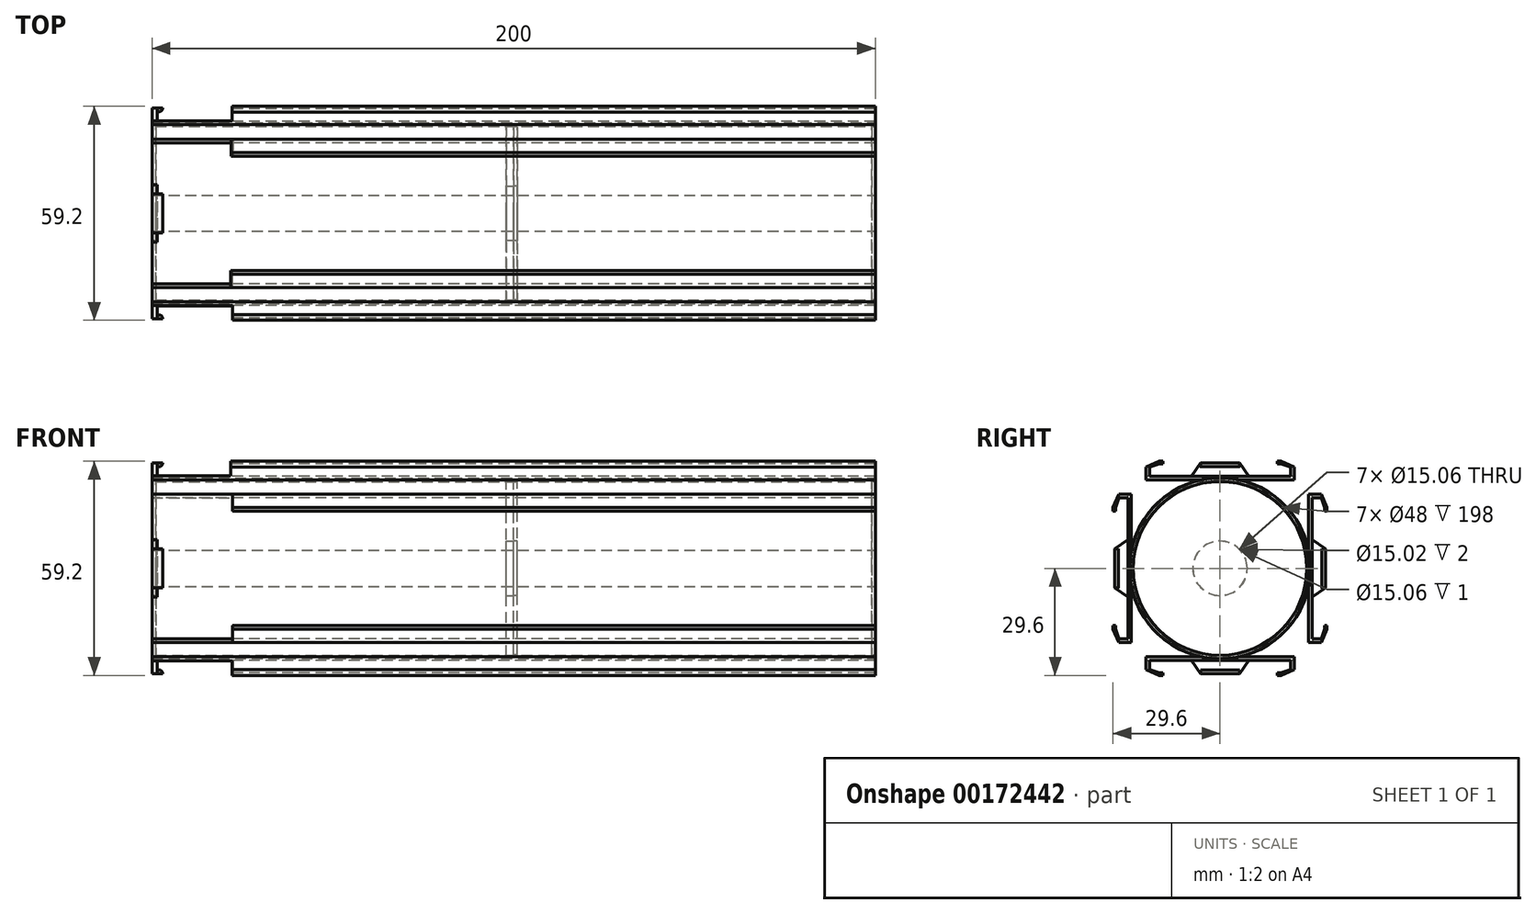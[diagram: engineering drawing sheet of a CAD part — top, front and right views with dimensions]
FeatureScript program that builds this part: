
annotation { "Feature Type Name" : "Feature", "Feature Type Description" : "" }
export const myFeature = defineFeature(function(context is Context, id is Id, definition is map)
    precondition{}
    {
        {
            var Q0;
            Q0=qCreatedBy(makeId("Top.planeOp"),FACE);
            var sketch = newSketch(context, id + "F0", { "sketchPlane" : qUnion([Q0])});
            skLineSegment(sketch, "E0", {"start": v(-100, 0) * mm, "end": v(-100, 25) * mm});
            skLineSegment(sketch, "E1", {"start": v(-100, 25) * mm, "end": v(100, 25) * mm});
            skLineSegment(sketch, "E2", {"start": v(100, 25) * mm, "end": v(100, 0) * mm});
            skLineSegment(sketch, "E3", {"start": v(100, 0) * mm, "end": v(-100, 0) * mm});
            skSolve(sketch);
        }
        {
            var Q0;
            Q0=makeQuery(id+"F0.imprint","IMPRINT",FACE,{"disambiguationData":[TD([[makeQuery(id+"F0.imprint","IMPRINT",EDGE,{"derivedFrom":sQuery(id+"F0.wireOp",EDGE,"E0")}),-1.0]])]});
            var Q1;
            Q1=sQuery(id+"F0.wireOp",EDGE,"E3");
            revolve(context, id + "F1", {"entities" : qUnion([Q0]), "axis" : qUnion([Q1]), "revolveType" : RevolveType.FULL});
        }
        {
            var Q0;
            Q0=qCreatedBy(makeId("Right.planeOp"),FACE);
            var sketch = newSketch(context, id + "F2", { "sketchPlane" : qUnion([Q0])});
            skLineSegment(sketch, "E4.top", {"start": v(20.5, 24.5) * mm, "end": v(-20.5, 24.5) * mm});
            skLineSegment(sketch, "E4.left", {"start": v(20.5, 28) * mm, "end": v(20.5, 24.5) * mm});
            skPoint(sketch, "E4.middle", {"position": v(0, 26.25) * mm});
            skLineSegment(sketch, "E5", {"start": v(19.5, 25.5) * mm, "end": v(0, 25.5) * mm});
            skLineSegment(sketch, "E6", {"start": v(19.5, 25.5) * mm, "end": v(19.5, 28) * mm});
            skLineSegment(sketch, "E7", {"start": v(20.93, 29.6) * mm, "end": v(1.4, 29.6) * mm, "construction": true});
            skLineSegment(sketch, "E8", {"start": v(20.5, 28) * mm, "end": v(16.8, 29.6) * mm});
            skLineSegment(sketch, "E9", {"start": v(16.8, 28.9) * mm, "end": v(19.5, 28) * mm});
            skLineSegment(sketch, "E10", {"start": v(16.8, 28.9) * mm, "end": v(22.6, 28.9) * mm, "construction": true});
            skLineSegment(sketch, "E11.MirrorCS", {"start": v(-19.5, 25.5) * mm, "end": v(0, 25.5) * mm});
            skLineSegment(sketch, "E12.MirrorCS", {"start": v(-16.8, 28.9) * mm, "end": v(-19.5, 28) * mm});
            skLineSegment(sketch, "E13.MirrorCS", {"start": v(-20.5, 28) * mm, "end": v(-16.8, 29.6) * mm});
            skLineSegment(sketch, "E14.MirrorCS", {"start": v(-20.5, 28) * mm, "end": v(-20.5, 24.5) * mm});
            skLineSegment(sketch, "E15.MirrorCS", {"start": v(-19.5, 25.5) * mm, "end": v(-19.5, 28) * mm});
            skLineSegment(sketch, "E16", {"start": v(16.87, 25.5) * mm, "end": v(16.8, 28.9) * mm, "construction": true});
            skLineSegment(sketch, "E17", {"start": v(16.8, 28.9) * mm, "end": v(15.8, 28.9) * mm});
            skLineSegment(sketch, "E18", {"start": v(15.8, 28.9) * mm, "end": v(15.8, 29.6) * mm});
            skLineSegment(sketch, "E19", {"start": v(15.8, 29.6) * mm, "end": v(16.8, 29.6) * mm});
            skLineSegment(sketch, "E20.MirrorCS", {"start": v(-20.93, 29.6) * mm, "end": v(-1.4, 29.6) * mm, "construction": true});
            skLineSegment(sketch, "E21.MirrorCS", {"start": v(-15.8, 28.9) * mm, "end": v(-15.8, 29.6) * mm});
            skLineSegment(sketch, "E22.MirrorCS", {"start": v(-16.8, 28.9) * mm, "end": v(-15.8, 28.9) * mm});
            skLineSegment(sketch, "E23", {"start": v(-15.8, 29.6) * mm, "end": v(-16.8, 29.6) * mm});
            skSolve(sketch);
        }
        {
            var Q0;
            Q0 = qSketchRegion(id + "F2", true);
            extrude(context, id + "F3", {"entities" : qUnion([Q0]), "operationType" : NewBodyOperationType.ADD, "endBound" : BoundingType.SYMMETRIC, "depth" : 200 * mm});
        }
        {
            var Q0;
            Q0=makeQuery(id+"F1.opRevolve","SWEPT_FACE",FACE,{"disambiguationData":[OSD([sQuery(id+"F0.wireOp",EDGE,"E0")])]});
            shell(context, id + "F4", {"entities" : qUnion([Q0]), "thickness" : 1 * mm});
        }
        {
            var Q0;
            Q0=qCreatedBy(makeId("Right.planeOp"),FACE);
            var sketch = newSketch(context, id + "F5", { "sketchPlane" : qUnion([Q0])});
            skCircle(sketch, "E24", {"center": v(0, 0) * mm, "radius": 24.27 * mm});
            skSolve(sketch);
        }
        {
            var Q0;
            Q0 = qSketchRegion(id + "F5", true);
            extrude(context, id + "F6", {"entities" : qUnion([Q0]), "oppositeDirection" : true, "depth" : 2 * mm});
        }
        {
            var Q0;
            Q0=makeQuery(id+"F6.opExtrude","CAP_FACE",FACE,{"disambiguationData":[OSD([sQuery(id+"F5.wireOp",EDGE,"E24")])],"isStart":true});
            var sketch = newSketch(context, id + "F7", { "sketchPlane" : qUnion([Q0])});
            skCircle(sketch, "E25", {"center": v(0, 0) * mm, "radius": 7.51 * mm});
            skSolve(sketch);
        }
        {
            var Q0;
            Q0 = qSketchRegion(id + "F7", true);
            extrude(context, id + "F8", {"entities" : qUnion([Q0]), "operationType" : NewBodyOperationType.REMOVE, "oppositeDirection" : true, "depth" : 5 * mm});
        }
        {
            var Q0;
            Q0=makeQuery(id+"F3.opExtrude","CAP_FACE",FACE,{"disambiguationData":[OSD([sQuery(id+"F2.wireOp",EDGE,"E4.top"),sQuery(id+"F2.wireOp",EDGE,"E4.left"),sQuery(id+"F2.wireOp",EDGE,"E5"),sQuery(id+"F2.wireOp",EDGE,"E6"),sQuery(id+"F2.wireOp",EDGE,"E8"),sQuery(id+"F2.wireOp",EDGE,"ZNRFgcwy-b1ID-LXQQ-LieV-oTXK7mRWD8L2"),sQuery(id+"F2.wireOp",EDGE,"E9"),sQuery(id+"F2.wireOp",EDGE,"E11.MirrorCS"),sQuery(id+"F2.wireOp",EDGE,"E12.MirrorCS"),sQuery(id+"F2.wireOp",EDGE,"bf2c11c1-d9c3-4b4b-aa85-f261bc206fdc0.MirrorCS"),sQuery(id+"F2.wireOp",EDGE,"E13.MirrorCS"),sQuery(id+"F2.wireOp",EDGE,"E14.MirrorCS"),sQuery(id+"F2.wireOp",EDGE,"E15.MirrorCS")])],"isStart":true});
            var sketch = newSketch(context, id + "F9", { "sketchPlane" : qUnion([Q0])});
            skLineSegment(sketch, "E26", {"start": v(0, 29.1) * mm, "end": v(-5.4, 29.1) * mm});
            skLineSegment(sketch, "E27", {"start": v(-5.4, 29.1) * mm, "end": v(-7.94, 25.5) * mm});
            skLineSegment(sketch, "E28.MirrorCS", {"start": v(0, 29.1) * mm, "end": v(5.4, 29.1) * mm});
            skLineSegment(sketch, "E29.MirrorCS", {"start": v(5.4, 29.1) * mm, "end": v(7.94, 25.5) * mm});
            skLineSegment(sketch, "E30", {"start": v(-7.94, 25.5) * mm, "end": v(7.94, 25.5) * mm});
            skSolve(sketch);
        }
        {
            var Q0;
            Q0=qCreatedBy(makeId("Right.planeOp"),FACE);
            var sketch = newSketch(context, id + "F10", { "sketchPlane" : qUnion([Q0])});
            skCircle(sketch, "E31", {"center": v(0, 0) * mm, "radius": 23.91 * mm});
            skSolve(sketch);
        }
        {
            var Q0;
            Q0 = qSketchRegion(id + "F10", true);
            extrude(context, id + "F11", {"entities" : qUnion([Q0]), "operationType" : NewBodyOperationType.ADD, "depth" : 1 * mm});
        }
        {
            var Q0;
            Q0=qCreatedBy(makeId("Right.planeOp"),FACE);
            var sketch = newSketch(context, id + "F12", { "sketchPlane" : qUnion([Q0])});
            skCircle(sketch, "E32", {"center": v(0, 0) * mm, "radius": 7.53 * mm});
            skSolve(sketch);
        }
        {
            var Q0;
            Q0 = qSketchRegion(id + "F12", true);
            extrude(context, id + "F13", {"entities" : qUnion([Q0]), "operationType" : NewBodyOperationType.REMOVE, "depth" : 2 * mm});
        }
        {
            var Q0;
            Q0=makeQuery(id+"F4.opShell","OFFSET_FACE",FACE,{"disambiguationData":[OSD([sQuery(id+"F0.wireOp",EDGE,"E2")])]});
            extrude(context, id + "F14", {"entities" : qUnion([Q0]), "oppositeDirection" : true, "depth" : 1 * mm});
        }
        {
            var Q0;
            Q0=makeQuery(id+"F1.opRevolve","SWEPT_FACE",FACE,{"disambiguationData":[OSD([sQuery(id+"F0.wireOp",EDGE,"E2")])]});
            var sketch = newSketch(context, id + "F15", { "sketchPlane" : qUnion([Q0])});
            skCircle(sketch, "E33", {"center": v(0, 0) * mm, "radius": 24.05 * mm});
            skSolve(sketch);
        }
        {
            var Q0;
            Q0 = qSketchRegion(id + "F15", true);
            extrude(context, id + "F16", {"entities" : qUnion([Q0]), "oppositeDirection" : true, "depth" : 1 * mm});
        }
        {
            var Q0;
            Q0=makeQuery(id+"F1.opRevolve","SWEPT_FACE",FACE,{"disambiguationData":[OSD([sQuery(id+"F0.wireOp",EDGE,"E0")])]});
            var sketch = newSketch(context, id + "F17", { "sketchPlane" : qUnion([Q0])});
            skCircle(sketch, "E34", {"center": v(0, 0) * mm, "radius": 24.2 * mm});
            skSolve(sketch);
        }
        {
            var Q0;
            Q0 = qSketchRegion(id + "F17", true);
            extrude(context, id + "F18", {"entities" : qUnion([Q0]), "operationType" : NewBodyOperationType.ADD, "oppositeDirection" : true, "depth" : 1 * mm});
        }
        {
            var Q0;
            Q0=makeQuery(id+"F18.boolean.opBoolean","MERGE",FACE,{"derivedFrom":[makeQuery(id+"F1.opRevolve","SWEPT_FACE",FACE,{"disambiguationData":[OSD([sQuery(id+"F0.wireOp",EDGE,"E0")])]}),makeQuery(id+"F18.opExtrude","CAP_FACE",FACE,{"disambiguationData":[OSD([sQuery(id+"F17.wireOp",EDGE,"E34")])],"isStart":true})]});
            var sketch = newSketch(context, id + "F19", { "sketchPlane" : qUnion([Q0])});
            skCircle(sketch, "E35", {"center": v(0, 0) * mm, "radius": 7.53 * mm});
            skSolve(sketch);
        }
        {
            var Q0;
            Q0 = qSketchRegion(id + "F19", true);
            extrude(context, id + "F20", {"entities" : qUnion([Q0]), "operationType" : NewBodyOperationType.REMOVE, "oppositeDirection" : true, "depth" : 2 * mm});
        }
        {
            var Q0;
            Q0 = qSketchRegion(id + "F9", true);
            extrude(context, id + "F21", {"entities" : qUnion([Q0]), "operationType" : NewBodyOperationType.ADD, "oppositeDirection" : true, "depth" : 1.5 * mm});
        }
        {
            var Q0;
            Q0=makeQuery(id+"F21.opExtrude","SWEPT_FACE",FACE,{"disambiguationData":[OSD([sQuery(id+"F9.wireOp",EDGE,"E26"),sQuery(id+"F9.wireOp",EDGE,"E28.MirrorCS")])]});
            var sketch = newSketch(context, id + "F22", { "sketchPlane" : qUnion([Q0])});
            skPoint(sketch, "E36.oppositeSnap0", {"position": v(-99.25, -5.4) * mm});
            skLineSegment(sketch, "E36.bottom", {"start": v(-100, 5.4) * mm, "end": v(-97.07, 5.4) * mm});
            skLineSegment(sketch, "E36.top", {"start": v(-100, -5.4) * mm, "end": v(-97.07, -5.4) * mm});
            skLineSegment(sketch, "E36.left", {"start": v(-100, 5.4) * mm, "end": v(-100, -5.4) * mm});
            skLineSegment(sketch, "E36.right", {"start": v(-97.07, 5.4) * mm, "end": v(-97.07, -5.4) * mm});
            skSolve(sketch);
        }
        {
            var Q0;
            Q0 = qSketchRegion(id + "F22", true);
            extrude(context, id + "F23", {"entities" : qUnion([Q0]), "operationType" : NewBodyOperationType.ADD, "oppositeDirection" : true, "depth" : 1 * mm});
        }
        {
            var Q0;
            Q0=makeQuery(id+"F23.opExtrude","CAP_EDGE",EDGE,{"disambiguationData":[OSD([sQuery(id+"F22.wireOp",EDGE,"E36.right")])],"isStart":false});
            fillet(context, id + "F24", {"entities" : qUnion([Q0]), "radius" : 1 * mm, "tangentPropagation" : true, "allowEdgeOverflow" : false});
        }
        {
            var Q0;
            Q0=makeQuery(id+"F14.opExtrude","SWEPT_BODY",BODY,{"disambiguationData":[OSD([sQuery(id+"F0.wireOp",EDGE,"E2"),sQuery(id+"F2.wireOp",EDGE,"E4.top"),sQuery(id+"F2.wireOp",EDGE,"E4.left"),sQuery(id+"F2.wireOp",EDGE,"E5"),sQuery(id+"F2.wireOp",EDGE,"E6"),sQuery(id+"F2.wireOp",EDGE,"E8"),sQuery(id+"F2.wireOp",EDGE,"ZNRFgcwy-b1ID-LXQQ-LieV-oTXK7mRWD8L2"),sQuery(id+"F2.wireOp",EDGE,"E9"),sQuery(id+"F2.wireOp",EDGE,"E11.MirrorCS"),sQuery(id+"F2.wireOp",EDGE,"E12.MirrorCS"),sQuery(id+"F2.wireOp",EDGE,"bf2c11c1-d9c3-4b4b-aa85-f261bc206fdc0.MirrorCS"),sQuery(id+"F2.wireOp",EDGE,"E13.MirrorCS"),sQuery(id+"F2.wireOp",EDGE,"E14.MirrorCS"),sQuery(id+"F2.wireOp",EDGE,"E15.MirrorCS")])]});
            var Q1;
            Q1=makeQuery(id+"F1.opRevolve","SWEPT_BODY",BODY,{"disambiguationData":[OSD([sQuery(id+"F0.wireOp",EDGE,"E0"),sQuery(id+"F0.wireOp",EDGE,"E1"),sQuery(id+"F0.wireOp",EDGE,"E2"),sQuery(id+"F0.wireOp",EDGE,"E3")])]});
            var Q2;
            Q2=makeQuery(id+"F1.opRevolve","SWEPT_FACE",FACE,{"disambiguationData":[OSD([sQuery(id+"F0.wireOp",EDGE,"E1")])]});
            circularPattern(context, id + "F25", {"entities" : qUnion([Q0, Q1]), "axis" : qUnion([Q2]), "angle" : 360 * degree, "instanceCount" : 4});
        }
        {
            var Q0;
            Q0=makeQuery(id+"F1.opRevolve","SWEPT_BODY",BODY,{"disambiguationData":[OSD([sQuery(id+"F0.wireOp",EDGE,"E0"),sQuery(id+"F0.wireOp",EDGE,"E1"),sQuery(id+"F0.wireOp",EDGE,"E2"),sQuery(id+"F0.wireOp",EDGE,"E3")])]});
            var Q1;
            Q1=makeQuery(id+"F1.opRevolve","SWEPT_FACE",FACE,{"disambiguationData":[OSD([sQuery(id+"F0.wireOp",EDGE,"E1")])]});
            circularPattern(context, id + "F26", {"entities" : qUnion([Q0]), "axis" : qUnion([Q1]), "angle" : 360 * degree, "instanceCount" : 4, "equalSpace" : true});
        }
        {
            var Q0;
            Q0=makeQuery(id+"F3.opExtrude","SWEPT_FACE",FACE,{"disambiguationData":[OSD([sQuery(id+"F2.wireOp",EDGE,"E14.MirrorCS")])]});
            var sketch = newSketch(context, id + "F27", { "sketchPlane" : qUnion([Q0])});
            skLineSegment(sketch, "E37.bottom", {"start": v(-100.21, 30.33) * mm, "end": v(-78.25, 30.33) * mm});
            skLineSegment(sketch, "E37.top", {"start": v(-100.21, 25.63) * mm, "end": v(-78.25, 25.63) * mm});
            skLineSegment(sketch, "E37.left", {"start": v(-100.21, 30.33) * mm, "end": v(-100.21, 25.63) * mm});
            skLineSegment(sketch, "E37.right", {"start": v(-78.25, 30.33) * mm, "end": v(-78.25, 25.63) * mm});
            skSolve(sketch);
        }
        {
            var Q0;
            Q0 = qSketchRegion(id + "F27", true);
            extrude(context, id + "F28", {"entities" : qUnion([Q0]), "operationType" : NewBodyOperationType.REMOVE, "oppositeDirection" : true, "depth" : 6 * mm});
        }
        {
            var Q0;
            Q0=makeQuery(id+"F3.opExtrude","SWEPT_FACE",FACE,{"disambiguationData":[OSD([sQuery(id+"F2.wireOp",EDGE,"E4.left")])]});
            var sketch = newSketch(context, id + "F29", { "sketchPlane" : qUnion([Q0])});
            skLineSegment(sketch, "E38.bottom", {"start": v(100, 25.6) * mm, "end": v(78.07, 25.6) * mm});
            skLineSegment(sketch, "E38.top", {"start": v(100, 29.9) * mm, "end": v(78.07, 29.9) * mm});
            skLineSegment(sketch, "E38.left", {"start": v(100, 25.6) * mm, "end": v(100, 29.9) * mm});
            skLineSegment(sketch, "E38.right", {"start": v(78.07, 25.6) * mm, "end": v(78.07, 29.9) * mm});
            skSolve(sketch);
        }
        {
            var Q0;
            Q0 = qSketchRegion(id + "F29", true);
            extrude(context, id + "F30", {"entities" : qUnion([Q0]), "operationType" : NewBodyOperationType.REMOVE, "oppositeDirection" : true, "depth" : 5 * mm});
        }
        {
            var Q0;
            Q0=makeQuery(id+"F26.opPattern","COPY",FACE,{"derivedFrom":makeQuery(id+"F3.opExtrude","SWEPT_FACE",FACE,{"disambiguationData":[OSD([sQuery(id+"F2.wireOp",EDGE,"E14.MirrorCS")])]}),"instanceName":"2"});
            var sketch = newSketch(context, id + "F31", { "sketchPlane" : qUnion([Q0])});
            skLineSegment(sketch, "E39.bottom", {"start": v(100, -25.5) * mm, "end": v(77.62, -25.5) * mm});
            skLineSegment(sketch, "E39.top", {"start": v(100, -29.75) * mm, "end": v(77.62, -29.75) * mm});
            skLineSegment(sketch, "E39.left", {"start": v(100, -25.5) * mm, "end": v(100, -29.75) * mm});
            skLineSegment(sketch, "E39.right", {"start": v(77.62, -25.5) * mm, "end": v(77.62, -29.75) * mm});
            skSolve(sketch);
        }
        {
            var Q0;
            Q0 = qSketchRegion(id + "F31", true);
            extrude(context, id + "F32", {"entities" : qUnion([Q0]), "operationType" : NewBodyOperationType.REMOVE, "oppositeDirection" : true, "depth" : 5 * mm});
        }
        {
            var Q0;
            Q0=makeQuery(id+"F26.opPattern","COPY",FACE,{"derivedFrom":makeQuery(id+"F3.opExtrude","SWEPT_FACE",FACE,{"disambiguationData":[OSD([sQuery(id+"F2.wireOp",EDGE,"E4.left")])]}),"instanceName":"2"});
            var sketch = newSketch(context, id + "F33", { "sketchPlane" : qUnion([Q0])});
            skLineSegment(sketch, "E40.bottom", {"start": v(-100, -25.57) * mm, "end": v(-77.86, -25.57) * mm});
            skLineSegment(sketch, "E40.top", {"start": v(-100, -30.06) * mm, "end": v(-77.86, -30.06) * mm});
            skLineSegment(sketch, "E40.left", {"start": v(-100, -25.57) * mm, "end": v(-100, -30.06) * mm});
            skLineSegment(sketch, "E40.right", {"start": v(-77.86, -25.57) * mm, "end": v(-77.86, -30.06) * mm});
            skSolve(sketch);
        }
        {
            var Q0;
            Q0 = qSketchRegion(id + "F33", true);
            extrude(context, id + "F34", {"entities" : qUnion([Q0]), "operationType" : NewBodyOperationType.REMOVE, "oppositeDirection" : true, "depth" : 5 * mm});
        }
        {
            var Q0;
            Q0=makeQuery(id+"F26.opPattern","COPY",FACE,{"derivedFrom":makeQuery(id+"F3.opExtrude","SWEPT_FACE",FACE,{"disambiguationData":[OSD([sQuery(id+"F2.wireOp",EDGE,"E14.MirrorCS")])]}),"instanceName":"1"});
            var sketch = newSketch(context, id + "F35", { "sketchPlane" : qUnion([Q0])});
            skLineSegment(sketch, "E41.bottom", {"start": v(-100, 25.61) * mm, "end": v(-77.74, 25.61) * mm});
            skLineSegment(sketch, "E41.top", {"start": v(-100, 30.26) * mm, "end": v(-77.74, 30.26) * mm});
            skLineSegment(sketch, "E41.left", {"start": v(-100, 25.61) * mm, "end": v(-100, 30.26) * mm});
            skLineSegment(sketch, "E41.right", {"start": v(-77.74, 25.61) * mm, "end": v(-77.74, 30.26) * mm});
            skSolve(sketch);
        }
        {
            var Q0;
            Q0 = qSketchRegion(id + "F35", true);
            extrude(context, id + "F36", {"entities" : qUnion([Q0]), "operationType" : NewBodyOperationType.REMOVE, "oppositeDirection" : true, "depth" : 5 * mm});
        }
        {
            var Q0;
            Q0=makeQuery(id+"F26.opPattern","COPY",FACE,{"derivedFrom":makeQuery(id+"F3.opExtrude","SWEPT_FACE",FACE,{"disambiguationData":[OSD([sQuery(id+"F2.wireOp",EDGE,"E14.MirrorCS")])]}),"instanceName":"3"});
            var sketch = newSketch(context, id + "F37", { "sketchPlane" : qUnion([Q0])});
            skLineSegment(sketch, "E42.bottom", {"start": v(-100, 25.52) * mm, "end": v(-77.82, 25.52) * mm});
            skLineSegment(sketch, "E42.top", {"start": v(-100, 29.95) * mm, "end": v(-77.82, 29.95) * mm});
            skLineSegment(sketch, "E42.left", {"start": v(-100, 25.52) * mm, "end": v(-100, 29.95) * mm});
            skLineSegment(sketch, "E42.right", {"start": v(-77.82, 25.52) * mm, "end": v(-77.82, 29.95) * mm});
            skSolve(sketch);
        }
        {
            var Q0;
            Q0 = qSketchRegion(id + "F37", true);
            extrude(context, id + "F38", {"entities" : qUnion([Q0]), "operationType" : NewBodyOperationType.REMOVE, "oppositeDirection" : true, "depth" : 5 * mm});
        }
        {
            var Q0;
            Q0=makeQuery(id+"F26.opPattern","COPY",FACE,{"derivedFrom":makeQuery(id+"F3.opExtrude","SWEPT_FACE",FACE,{"disambiguationData":[OSD([sQuery(id+"F2.wireOp",EDGE,"E4.left")])]}),"instanceName":"3"});
            var sketch = newSketch(context, id + "F39", { "sketchPlane" : qUnion([Q0])});
            skLineSegment(sketch, "E43.bottom", {"start": v(-100, -25.56) * mm, "end": v(-77.82, -25.56) * mm});
            skLineSegment(sketch, "E43.top", {"start": v(-100, -29.92) * mm, "end": v(-77.82, -29.92) * mm});
            skLineSegment(sketch, "E43.left", {"start": v(-100, -25.56) * mm, "end": v(-100, -29.92) * mm});
            skLineSegment(sketch, "E43.right", {"start": v(-77.82, -25.56) * mm, "end": v(-77.82, -29.92) * mm});
            skSolve(sketch);
        }
        {
            var Q0;
            Q0 = qSketchRegion(id + "F39", true);
            extrude(context, id + "F40", {"entities" : qUnion([Q0]), "operationType" : NewBodyOperationType.REMOVE, "oppositeDirection" : true, "depth" : 5 * mm});
        }
        {
            var Q0;
            Q0=makeQuery(id+"F26.opPattern","COPY",FACE,{"derivedFrom":makeQuery(id+"F3.opExtrude","SWEPT_FACE",FACE,{"disambiguationData":[OSD([sQuery(id+"F2.wireOp",EDGE,"E4.left")])]}),"instanceName":"1"});
            var sketch = newSketch(context, id + "F41", { "sketchPlane" : qUnion([Q0])});
            skLineSegment(sketch, "E44.bottom", {"start": v(-100, -25.5) * mm, "end": v(-77.8, -25.5) * mm});
            skLineSegment(sketch, "E44.top", {"start": v(-100, -30.2) * mm, "end": v(-77.8, -30.2) * mm});
            skLineSegment(sketch, "E44.left", {"start": v(-100, -25.5) * mm, "end": v(-100, -30.2) * mm});
            skLineSegment(sketch, "E44.right", {"start": v(-77.8, -25.5) * mm, "end": v(-77.8, -30.2) * mm});
            skSolve(sketch);
        }
        {
            var Q0;
            Q0 = qSketchRegion(id + "F41", true);
            extrude(context, id + "F42", {"entities" : qUnion([Q0]), "operationType" : NewBodyOperationType.REMOVE, "oppositeDirection" : true, "depth" : 5 * mm});
        }
    });
